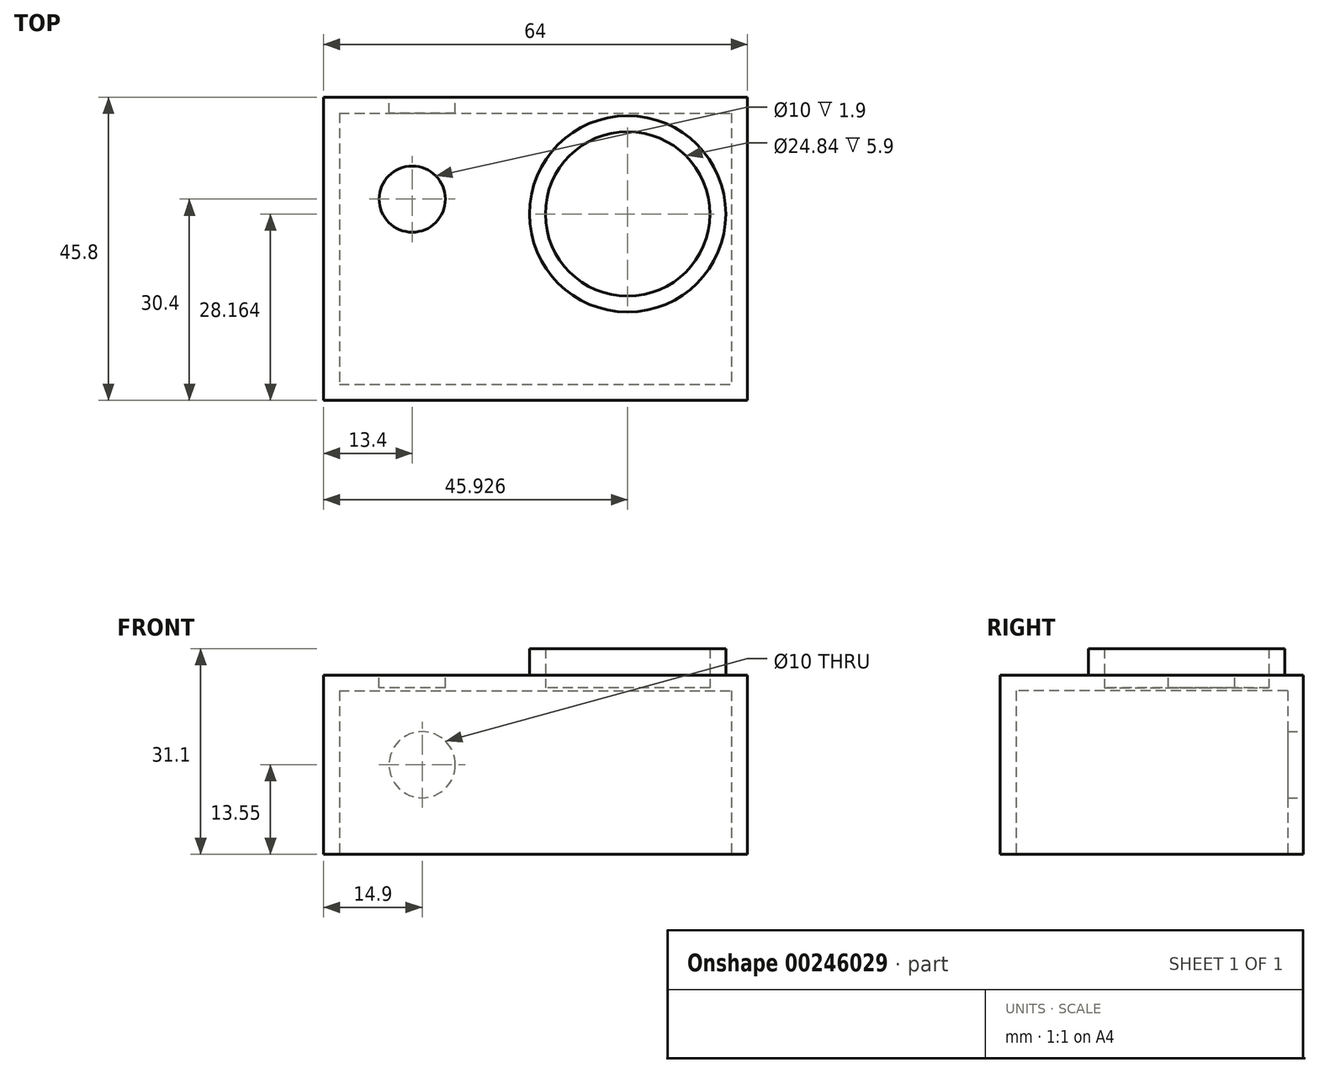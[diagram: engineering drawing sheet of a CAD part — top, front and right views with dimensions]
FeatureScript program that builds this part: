
annotation { "Feature Type Name" : "Feature", "Feature Type Description" : "" }
export const myFeature = defineFeature(function(context is Context, id is Id, definition is map)
    precondition{}
    {
        {
            assignVariable(context, id + "F0", {"name" : "goproThickness", "anyValue" : 24.7});
        }
        {
            assignVariable(context, id + "F1", {"name" : "lensDepth", "anyValue" : 4});
        }
        {
            assignVariable(context, id + "F2", {"name" : "caseThickness", "anyValue" : 2.4});
        }
        {
            assignVariable(context, id + "F3", {"name" : "webThickness", "anyValue" : 0.5});
        }
        {
            var Q0;
            Q0=qCreatedBy(makeId("Top.planeOp"),FACE);
            var sketch = newSketch(context, id + "F4", { "sketchPlane" : qUnion([Q0])});
            skLineSegment(sketch, "E0.bottom", {"start": v(-29.6, 20.5) * mm, "end": v(29.6, 20.5) * mm});
            skLineSegment(sketch, "E0.top", {"start": v(-29.6, -20.5) * mm, "end": v(29.6, -20.5) * mm});
            skLineSegment(sketch, "E0.left", {"start": v(-29.6, 20.5) * mm, "end": v(-29.6, -20.5) * mm});
            skLineSegment(sketch, "E0.right", {"start": v(29.6, 20.5) * mm, "end": v(29.6, -20.5) * mm});
            skPoint(sketch, "E0.middle", {"position": v(0, 0) * mm});
            skLineSegment(sketch, "E1.0", {"start": v(-32, 22.9) * mm, "end": v(32, 22.9) * mm});
            skLineSegment(sketch, "E1.1", {"start": v(-32, 22.9) * mm, "end": v(-32, -22.9) * mm});
            skLineSegment(sketch, "E1.2", {"start": v(-32, -22.9) * mm, "end": v(32, -22.9) * mm});
            skLineSegment(sketch, "E1.3", {"start": v(32, 22.9) * mm, "end": v(32, -22.9) * mm});
            skSolve(sketch);
        }
        {
            var Q0;
            Q0=qSketchRegion(id+"F4",true);
            extrude(context, id + "F5", {"entities" : qUnion([Q0]), "depth" : (getVariable(context, 'goproThickness')) * mm});
        }
        {
            var Q0;
            Q0=makeQuery(id+"F5.opExtrude","CAP_FACE",FACE,{"disambiguationData":[OSD([sQuery(id+"F4.wireOp",EDGE,"E0.bottom"),sQuery(id+"F4.wireOp",EDGE,"E0.top"),sQuery(id+"F4.wireOp",EDGE,"E0.left"),sQuery(id+"F4.wireOp",EDGE,"E0.right"),sQuery(id+"F4.wireOp",EDGE,"E1.0"),sQuery(id+"F4.wireOp",EDGE,"E1.1"),sQuery(id+"F4.wireOp",EDGE,"E1.2"),sQuery(id+"F4.wireOp",EDGE,"E1.3")])],"isStart":false});
            var sketch = newSketch(context, id + "F6", { "sketchPlane" : qUnion([Q0])});
            skLineSegment(sketch, "E2.bottom", {"start": v(-29.6, 20.5) * mm, "end": v(29.6, 20.5) * mm});
            skLineSegment(sketch, "E2.top", {"start": v(-29.6, -20.5) * mm, "end": v(29.6, -20.5) * mm});
            skLineSegment(sketch, "E2.left", {"start": v(-29.6, 20.5) * mm, "end": v(-29.6, -20.5) * mm});
            skLineSegment(sketch, "E2.right", {"start": v(29.6, 20.5) * mm, "end": v(29.6, -20.5) * mm});
            skPoint(sketch, "E2.middle", {"position": v(0, 0) * mm});
            skLineSegment(sketch, "E3.bottom", {"start": v(-32, 22.9) * mm, "end": v(32, 22.9) * mm});
            skLineSegment(sketch, "E3.top", {"start": v(-32, -22.9) * mm, "end": v(32, -22.9) * mm});
            skLineSegment(sketch, "E3.left", {"start": v(-32, 22.9) * mm, "end": v(-32, -22.9) * mm});
            skLineSegment(sketch, "E3.right", {"start": v(32, 22.9) * mm, "end": v(32, -22.9) * mm});
            skSolve(sketch);
        }
        {
            var Q0;
            Q0=qSketchRegion(id+"F6",true);
            var Q1;
            Q1=makeQuery(id+"F6.imprint","IMPRINT",FACE,{"disambiguationData":[TD([[makeQuery(id+"F6.imprint","IMPRINT",EDGE,{"derivedFrom":sQuery(id+"F6.wireOp",EDGE,"E2.bottom")}),-1.0]])]});
            extrude(context, id + "F7", {"entities" : qUnion([Q0, Q1]), "operationType" : NewBodyOperationType.ADD, "depth" : (getVariable(context, 'caseThickness')) * mm, "offsetDistance" : 25 * mm});
        }
        {
            var Q0;
            Q0=makeQuery(id+"F7.opExtrude","CAP_FACE",FACE,{"disambiguationData":[OSD([sQuery(id+"F6.wireOp",EDGE,"E3.bottom"),sQuery(id+"F6.wireOp",EDGE,"E3.top"),sQuery(id+"F6.wireOp",EDGE,"E3.left"),sQuery(id+"F6.wireOp",EDGE,"E3.right")])],"isStart":false});
            var sketch = newSketch(context, id + "F8", { "sketchPlane" : qUnion([Q0])});
            skCircle(sketch, "E4", {"center": v(-18.6, 7.5) * mm, "radius": 5 * mm});
            skSolve(sketch);
        }
        {
            var Q0;
            Q0=qSketchRegion(id+"F8",true);
            extrude(context, id + "F9", {"entities" : qUnion([Q0]), "operationType" : NewBodyOperationType.REMOVE, "oppositeDirection" : true, "depth" : (getVariable(context, 'caseThickness') - getVariable(context, 'webThickness')) * mm});
        }
        {
            var Q0;
            Q0=makeQuery(id+"F7.opExtrude","CAP_FACE",FACE,{"disambiguationData":[OSD([sQuery(id+"F6.wireOp",EDGE,"E3.bottom"),sQuery(id+"F6.wireOp",EDGE,"E3.top"),sQuery(id+"F6.wireOp",EDGE,"E3.left"),sQuery(id+"F6.wireOp",EDGE,"E3.right")])],"isStart":false});
            var sketch = newSketch(context, id + "F10", { "sketchPlane" : qUnion([Q0])});
            skCircle(sketch, "E5", {"center": v(13.93, 5.26) * mm, "radius": 12.42 * mm});
            skCircle(sketch, "E6", {"center": v(13.93, 5.26) * mm, "radius": 14.82 * mm});
            skSolve(sketch);
        }
        {
            var Q0;
            Q0=qSketchRegion(id+"F10",true);
            extrude(context, id + "F11", {"entities" : qUnion([Q0]), "operationType" : NewBodyOperationType.ADD, "depth" : (getVariable(context, 'lensDepth')) * mm});
        }
        {
            var Q0;
            Q0=makeQuery(id+"F11.boolean.opBoolean","SPLIT",FACE,{"disambiguationData":[TD([makeQuery(id+"F11.opExtrude","SWEPT_FACE",FACE,{"disambiguationData":[OSD([sQuery(id+"F10.wireOp",EDGE,"E5")])]})])],"derivedFrom":makeQuery(id+"F7.opExtrude","CAP_FACE",FACE,{"disambiguationData":[OSD([sQuery(id+"F6.wireOp",EDGE,"E3.bottom"),sQuery(id+"F6.wireOp",EDGE,"E3.top"),sQuery(id+"F6.wireOp",EDGE,"E3.left"),sQuery(id+"F6.wireOp",EDGE,"E3.right")])],"isStart":false})});
            extrude(context, id + "F12", {"entities" : qUnion([Q0]), "operationType" : NewBodyOperationType.REMOVE, "oppositeDirection" : true, "depth" : (getVariable(context, 'caseThickness') - getVariable(context, 'webThickness')) * mm});
        }
        {
            var Q0;
            Q0=makeQuery(id+"F7.boolean.opBoolean","MERGE",FACE,{"derivedFrom":[makeQuery(id+"F5.opExtrude","SWEPT_FACE",FACE,{"disambiguationData":[OSD([sQuery(id+"F4.wireOp",EDGE,"E1.0")])]}),makeQuery(id+"F7.opExtrude","SWEPT_FACE",FACE,{"disambiguationData":[OSD([sQuery(id+"F6.wireOp",EDGE,"E3.bottom")])]})]});
            var sketch = newSketch(context, id + "F13", { "sketchPlane" : qUnion([Q0])});
            skCircle(sketch, "E7", {"center": v(17.1, 13.55) * mm, "radius": 5 * mm});
            skPoint(sketch, "E7.centerSnap0", {"position": v(32, 13.55) * mm});
            skSolve(sketch);
        }
        {
            var Q0;
            Q0=qSketchRegion(id+"F13",true);
            extrude(context, id + "F14", {"entities" : qUnion([Q0]), "operationType" : NewBodyOperationType.REMOVE, "oppositeDirection" : true, "depth" : (getVariable(context, 'caseThickness')) * mm});
        }
        {
            var Q0;
            Q0=makeQuery(id+"F11.opExtrude","CAP_FACE",FACE,{"disambiguationData":[OSD([sQuery(id+"F10.wireOp",EDGE,"E5"),sQuery(id+"F10.wireOp",EDGE,"E6")])],"isStart":false});
            cPlane(context, id + "F15", {"entities" : qUnion([Q0]), "cplaneType" : CPlaneType.OFFSET, "offset" : 0 * mm, "width" : 150 * mm, "height" : 150 * mm});
        }
    });
